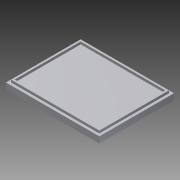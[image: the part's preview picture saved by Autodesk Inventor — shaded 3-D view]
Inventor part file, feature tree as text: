
AUTODESK INVENTOR PART (.ipt)
format: ipt  version: 2016 (Build 200138000, 138)  size: 91,648 bytes
history: native  units: mm
features: extrude x2, sketch x2
ambient origin geometry x8: Origin, YZ Plane, XZ Plane, XY Plane, X Axis, Y Axis, Z Axis, Center Point
bodies: Solid1 (feature_tree)
feature tree (4):
  extrude  "Extrusion1"  Depth=120.0mm
  extrude  "Extrusion2"  Depth=4.0mm
  sketch  "Sketch1"  dims[d0=150.0mm d1=120.0mm]
  sketch  "Sketch2"  dims[d2=10.0mm d3=0.0mm d4=4.0mm d5=4.0mm d6=3.0mm d7=3.0mm d8=4.0mm d9=0.0mm]
